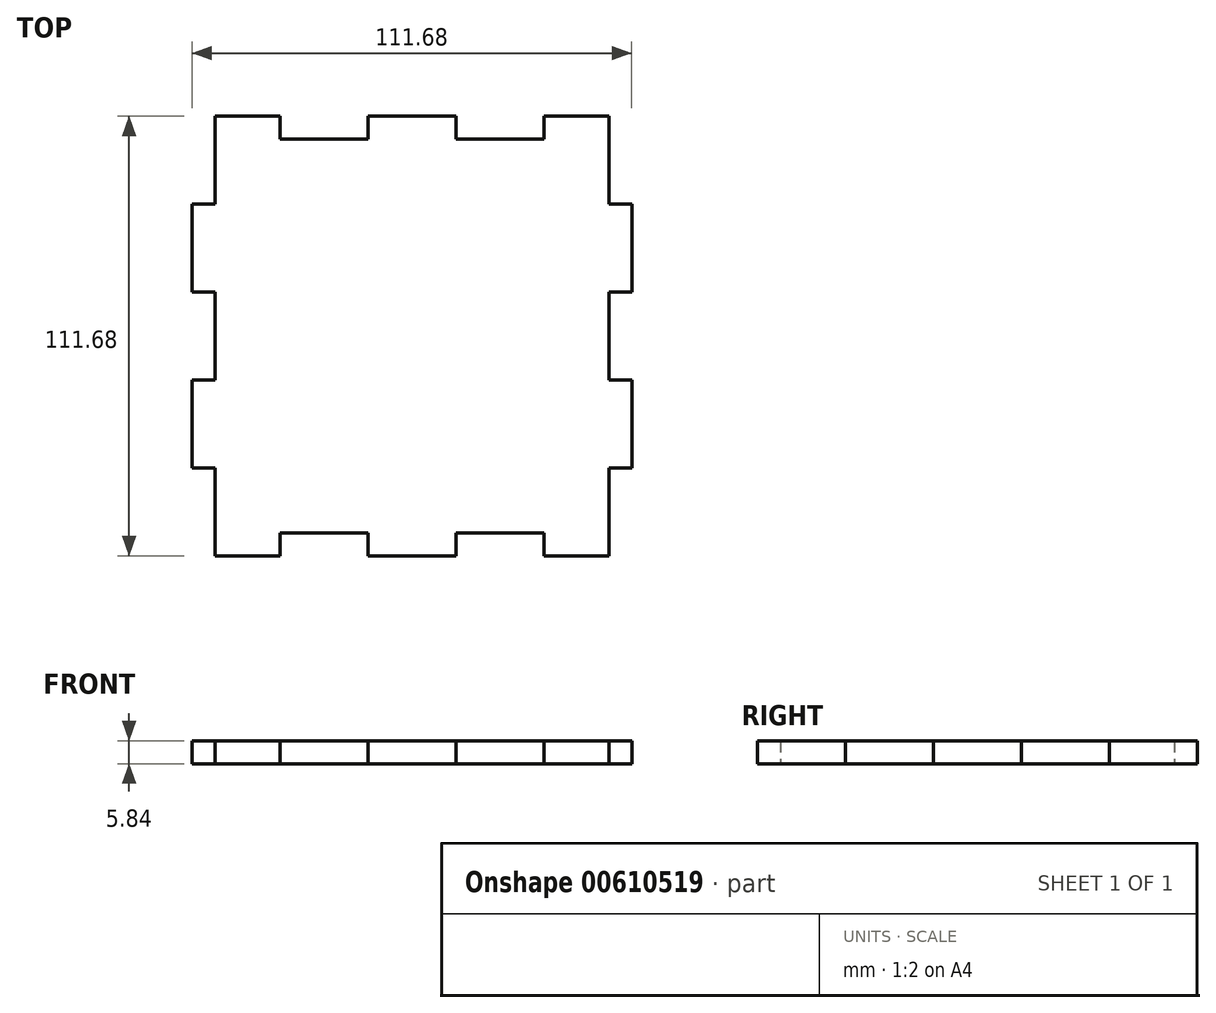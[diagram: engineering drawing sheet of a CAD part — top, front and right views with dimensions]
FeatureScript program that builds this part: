
annotation { "Feature Type Name" : "Feature", "Feature Type Description" : "" }
export const myFeature = defineFeature(function(context is Context, id is Id, definition is map)
    precondition{}
    {
        {
            var Q0;
            Q0=qCreatedBy(makeId("Top.planeOp"),FACE);
            var sketch = newSketch(context, id + "F0", { "sketchPlane" : qUnion([Q0])});
            skLineSegment(sketch, "E0.bottom", {"start": v(-50, 50) * mm, "end": v(50, 50) * mm});
            skLineSegment(sketch, "E0.top", {"start": v(-50, -50) * mm, "end": v(50, -50) * mm});
            skLineSegment(sketch, "E0.left", {"start": v(-50, 50) * mm, "end": v(-50, -50) * mm});
            skLineSegment(sketch, "E0.right", {"start": v(50, 50) * mm, "end": v(50, -50) * mm});
            skLineSegment(sketch, "E1.bottom", {"start": v(-50, 55.84) * mm, "end": v(-33.5, 55.84) * mm});
            skLineSegment(sketch, "E1.top", {"start": v(-50, -55.84) * mm, "end": v(-33.5, -55.84) * mm});
            skPoint(sketch, "E1.middle", {"position": v(0, 0) * mm});
            skLineSegment(sketch, "E2", {"start": v(-33.5, 50) * mm, "end": v(-33.5, 55.84) * mm});
            skLineSegment(sketch, "E3", {"start": v(-11.17, 50) * mm, "end": v(-11.17, 55.84) * mm});
            skLineSegment(sketch, "E4", {"start": v(11.17, 50) * mm, "end": v(11.17, 55.84) * mm});
            skLineSegment(sketch, "E5", {"start": v(33.5, 50) * mm, "end": v(33.5, 55.84) * mm});
            skLineSegment(sketch, "E6.trimOffspring", {"start": v(-11.17, 55.84) * mm, "end": v(11.17, 55.84) * mm});
            skLineSegment(sketch, "E7.trimOffspring", {"start": v(33.5, 55.84) * mm, "end": v(50, 55.84) * mm});
            skLineSegment(sketch, "E8", {"start": v(-50, 33.5) * mm, "end": v(-55.84, 33.5) * mm});
            skLineSegment(sketch, "E9", {"start": v(-50, 11.17) * mm, "end": v(-55.84, 11.17) * mm});
            skLineSegment(sketch, "E10", {"start": v(-50, -11.17) * mm, "end": v(-55.84, -11.17) * mm});
            skLineSegment(sketch, "E11", {"start": v(-50, -33.5) * mm, "end": v(-55.84, -33.5) * mm});
            skLineSegment(sketch, "E12", {"start": v(-33.5, -50) * mm, "end": v(-33.5, -55.84) * mm});
            skLineSegment(sketch, "E13", {"start": v(-11.17, -50) * mm, "end": v(-11.17, -55.84) * mm});
            skLineSegment(sketch, "E14", {"start": v(11.17, -50) * mm, "end": v(11.17, -55.84) * mm});
            skLineSegment(sketch, "E15", {"start": v(33.5, -50) * mm, "end": v(33.5, -55.84) * mm});
            skLineSegment(sketch, "E16.trimOffspring", {"start": v(-11.17, -55.84) * mm, "end": v(11.17, -55.84) * mm});
            skLineSegment(sketch, "E17.trimOffspring", {"start": v(33.5, -55.84) * mm, "end": v(50, -55.84) * mm});
            skLineSegment(sketch, "E18", {"start": v(50, -33.5) * mm, "end": v(55.84, -33.5) * mm});
            skLineSegment(sketch, "E19", {"start": v(50, -11.17) * mm, "end": v(55.84, -11.17) * mm});
            skLineSegment(sketch, "E20", {"start": v(50, 11.17) * mm, "end": v(55.84, 11.17) * mm});
            skLineSegment(sketch, "E21", {"start": v(50, 33.5) * mm, "end": v(55.84, 33.5) * mm});
            skLineSegment(sketch, "E22", {"start": v(-55.84, -11.17) * mm, "end": v(-55.84, -33.5) * mm});
            skLineSegment(sketch, "E23", {"start": v(-55.84, 33.5) * mm, "end": v(-55.84, 11.17) * mm});
            skLineSegment(sketch, "E24", {"start": v(55.84, 33.5) * mm, "end": v(55.84, 11.17) * mm});
            skLineSegment(sketch, "E25", {"start": v(55.84, -11.17) * mm, "end": v(55.84, -33.5) * mm});
            skLineSegment(sketch, "E26", {"start": v(-50, 50) * mm, "end": v(-50, 55.84) * mm});
            skLineSegment(sketch, "E27", {"start": v(50, 50) * mm, "end": v(50, 55.84) * mm});
            skLineSegment(sketch, "E28", {"start": v(-50, -50) * mm, "end": v(-50, -55.84) * mm});
            skLineSegment(sketch, "E29", {"start": v(50, -50) * mm, "end": v(50, -55.84) * mm});
            skPoint(sketch, "E30.orphan", {"position": v(-55.84, 55.84) * mm});
            skPoint(sketch, "E31.orphan", {"position": v(55.84, 55.84) * mm});
            skPoint(sketch, "E32.orphan", {"position": v(55.84, -55.84) * mm});
            skPoint(sketch, "E33.orphan", {"position": v(-55.84, -55.84) * mm});
            skSolve(sketch);
        }
        {
            var Q0;
            Q0=qSketchRegion(id+"F0",true);
            extrude(context, id + "F1", {"entities" : qUnion([Q0]), "depth" : 5.84 * mm, "offsetDistance" : 25 * mm});
        }
    });
